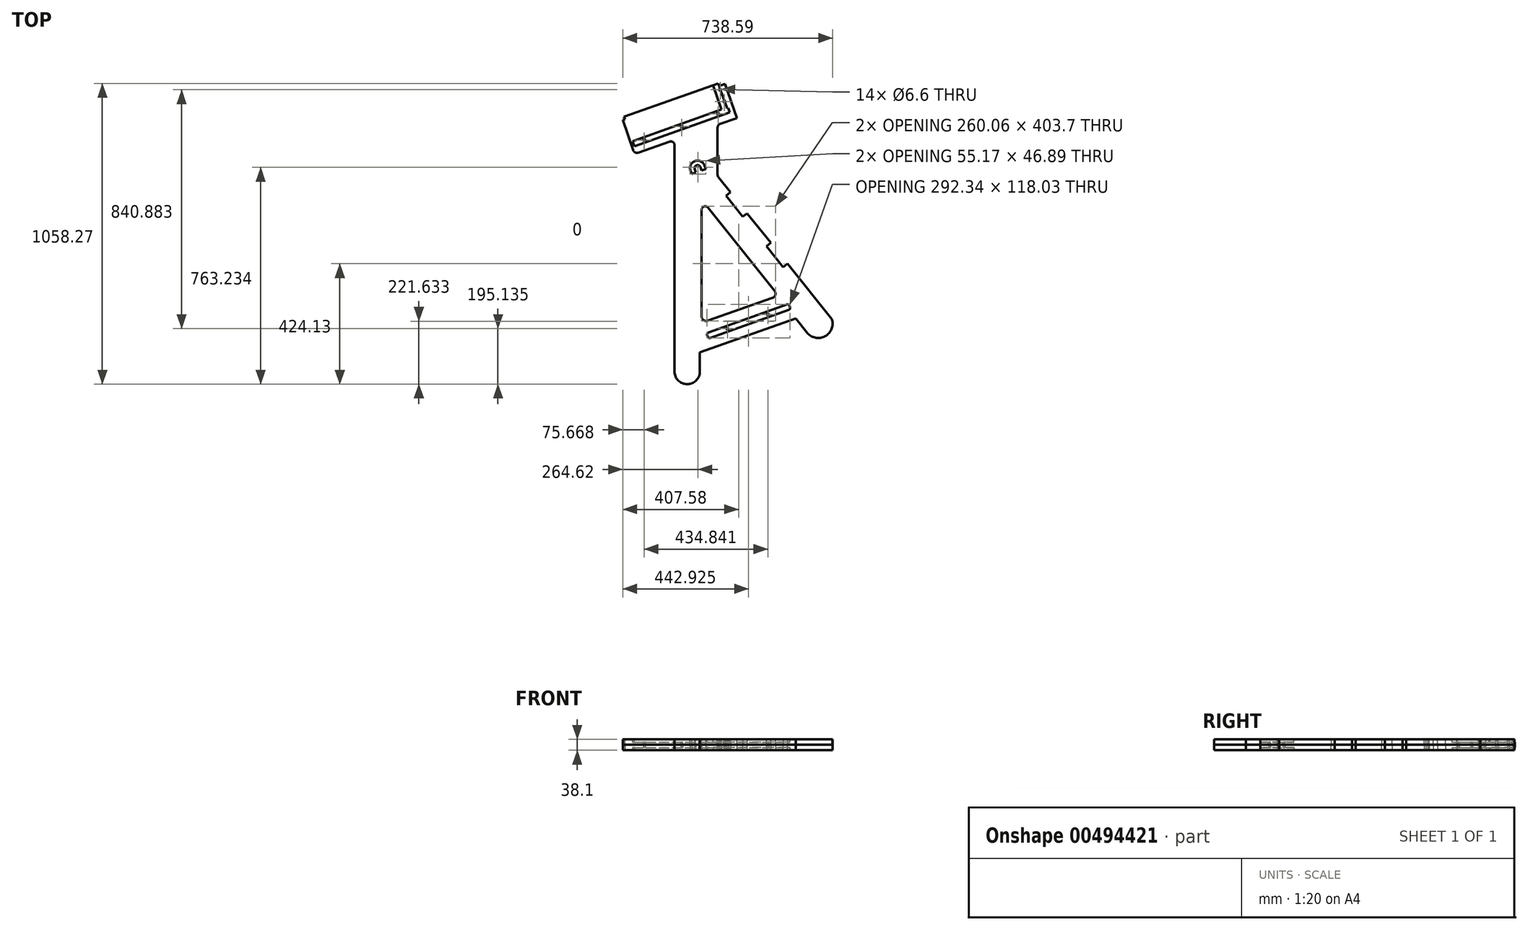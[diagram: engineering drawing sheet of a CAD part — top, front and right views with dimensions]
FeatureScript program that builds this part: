
annotation { "Feature Type Name" : "Feature", "Feature Type Description" : "" }
export const myFeature = defineFeature(function(context is Context, id is Id, definition is map)
    precondition{}
    {
        {
            var Q0;
            Q0=qCreatedBy(makeId("Top.planeOp"),FACE);
            var sketch = newSketch(context, id + "F0", { "sketchPlane" : qUnion([Q0])});
            skLineSegment(sketch, "E0", {"start": v(-306.62, -10.3) * mm, "end": v(-306.88, -10.27) * mm});
            skLineSegment(sketch, "E1", {"start": v(727.27, -289.32) * mm, "end": v(727.27, 507.63) * mm});
            skPoint(sketch, "E2.visualSharp", {"position": v(727.27, -334.1) * mm});
            skPoint(sketch, "E3.visualSharp", {"position": v(828.87, -334.66) * mm});
            skLineSegment(sketch, "E4", {"start": v(878.9, 569.94) * mm, "end": v(878.9, 402.04) * mm});
            skLineSegment(sketch, "E5", {"start": v(710.35, 519.6) * mm, "end": v(599.11, 480.45) * mm});
            skLineSegment(sketch, "E6", {"start": v(582.92, 488.22) * mm, "end": v(544.97, 596.03) * mm});
            skLineSegment(sketch, "E7", {"start": v(544.97, 596.03) * mm, "end": v(552.9, 598.83) * mm});
            skLineSegment(sketch, "E8", {"start": v(904.35, 722.53) * mm, "end": v(946.52, 602.74) * mm});
            skLineSegment(sketch, "E9", {"start": v(887.38, 581.92) * mm, "end": v(946.52, 602.74) * mm});
            skLineSegment(sketch, "E10", {"start": v(822.52, -95.2) * mm, "end": v(822.52, 279.38) * mm});
            skLineSegment(sketch, "E11", {"start": v(845.13, 287.31) * mm, "end": v(1078.98, -4.96) * mm});
            skPoint(sketch, "E12.visualSharp", {"position": v(822.52, 315.58) * mm});
            skArc(sketch, "E12.filletArc", {"start": v(845.13, 287.31) * mm, "mid": v(831.01, 291.36) * mm, "end": v(822.52, 279.38) * mm});
            skLineSegment(sketch, "E13", {"start": v(587.13, 476.24) * mm, "end": v(946.52, 602.74) * mm, "construction": true});
            skLineSegment(sketch, "E14", {"start": v(881.68, 394.1) * mm, "end": v(1281.26, -105.33) * mm});
            skArc(sketch, "E15", {"start": v(1192.97, -152.23) * mm, "mid": v(1256.56, -165.38) * mm, "end": v(1281.26, -105.33) * mm});
            skLineSegment(sketch, "E16", {"start": v(816.46, -289.32) * mm, "end": v(816.46, -221.63) * mm});
            skLineSegment(sketch, "E17", {"start": v(926.55, 733.52) * mm, "end": v(1268.68, -238.42) * mm, "construction": true});
            skPoint(sketch, "E18.visualSharp", {"position": v(878.9, 397.58) * mm});
            skArc(sketch, "E18.filletArc", {"start": v(878.9, 402.04) * mm, "mid": v(879.61, 397.83) * mm, "end": v(881.68, 394.1) * mm});
            skPoint(sketch, "E19.visualSharp", {"position": v(878.9, 578.94) * mm});
            skArc(sketch, "E19.filletArc", {"start": v(887.38, 581.92) * mm, "mid": v(881.23, 577.28) * mm, "end": v(878.9, 569.94) * mm});
            skArc(sketch, "E20.filletArc", {"start": v(727.27, 507.63) * mm, "mid": v(721.9, 518) * mm, "end": v(710.35, 519.6) * mm});
            skLineSegment(sketch, "E21", {"start": v(549.74, 607.81) * mm, "end": v(880.86, 724.36) * mm});
            skLineSegment(sketch, "E22", {"start": v(549.74, 607.81) * mm, "end": v(552.9, 598.83) * mm});
            skLineSegment(sketch, "E23", {"start": v(880.86, 724.36) * mm, "end": v(884.02, 715.38) * mm});
            skLineSegment(sketch, "E24.trimOffspring", {"start": v(884.02, 715.38) * mm, "end": v(904.35, 722.53) * mm, "construction": true});
            skLineSegment(sketch, "E25.trimOffspring", {"start": v(884.02, 715.38) * mm, "end": v(904.35, 722.53) * mm});
            skLineSegment(sketch, "E26", {"start": v(544.97, 596.03) * mm, "end": v(903.18, -421.63) * mm, "construction": true});
            skLineSegment(sketch, "E27", {"start": v(869.21, -325.12) * mm, "end": v(1232.7, -197.18) * mm, "construction": true});
            skLineSegment(sketch, "E28", {"start": v(816.46, -221.63) * mm, "end": v(1153.56, -102.97) * mm});
            skLineSegment(sketch, "E29", {"start": v(844.5, -110.78) * mm, "end": v(1071.57, -30.85) * mm});
            skArc(sketch, "E30", {"start": v(727.27, -289.32) * mm, "mid": v(771.86, -333.91) * mm, "end": v(816.46, -289.32) * mm});
            skPoint(sketch, "E31.visualSharp", {"position": v(587.13, 476.24) * mm});
            skArc(sketch, "E31.filletArc", {"start": v(582.92, 488.22) * mm, "mid": v(589.4, 480.98) * mm, "end": v(599.11, 480.45) * mm});
            skPoint(sketch, "E32.visualSharp", {"position": v(1093.5, -23.13) * mm});
            skArc(sketch, "E32.filletArc", {"start": v(1071.57, -30.85) * mm, "mid": v(1081.96, -19.82) * mm, "end": v(1078.98, -4.96) * mm});
            skPoint(sketch, "E33.visualSharp", {"position": v(822.52, -118.52) * mm});
            skArc(sketch, "E33.filletArc", {"start": v(822.52, -95.2) * mm, "mid": v(829.49, -108.68) * mm, "end": v(844.5, -110.78) * mm});
            skLineSegment(sketch, "E34", {"start": v(1153.56, -102.97) * mm, "end": v(1192.97, -152.23) * mm});
            skPoint(sketch, "E35", {"position": v(1256.56, -165.38) * mm});
            skPoint(sketch, "E36", {"position": v(771.86, -333.91) * mm});
            skPoint(sketch, "E37", {"position": v(1272.05, -152.68) * mm});
            skLineSegment(sketch, "E38", {"start": v(786.67, -331.38) * mm, "end": v(1249.58, -168.44) * mm, "construction": true});
            skArc(sketch, "E39", {"start": v(817.98, 430.01) * mm, "mid": v(804.77, 436.34) * mm, "end": v(798.43, 423.13) * mm});
            skArc(sketch, "E40", {"start": v(832.96, 435.28) * mm, "mid": v(799.5, 451.32) * mm, "end": v(783.46, 417.86) * mm});
            skLineSegment(sketch, "E41", {"start": v(783.46, 417.86) * mm, "end": v(787.67, 405.88) * mm});
            skLineSegment(sketch, "E42", {"start": v(787.67, 405.88) * mm, "end": v(802.65, 411.15) * mm});
            skLineSegment(sketch, "E43", {"start": v(802.65, 411.15) * mm, "end": v(798.43, 423.13) * mm});
            skLineSegment(sketch, "E44", {"start": v(817.98, 430.01) * mm, "end": v(822.2, 418.03) * mm});
            skLineSegment(sketch, "E45", {"start": v(822.2, 418.03) * mm, "end": v(837.17, 423.3) * mm});
            skLineSegment(sketch, "E46", {"start": v(837.17, 423.3) * mm, "end": v(832.96, 435.28) * mm});
            skSolve(sketch);
        }
        {
            var Q0;
            Q0=makeQuery(id+"F0.imprint","IMPRINT",FACE,{"disambiguationData":[TD([[makeQuery(id+"F0.imprint","IMPRINT",EDGE,{"derivedFrom":sQuery(id+"F0.wireOp",EDGE,"oAVC5DI8-kh1G-Qbfy-uwvq-Txyh6lFHP0Ui")}),1.0]])]});
            var Q1;
            Q1=makeQuery(id+"F0.imprint","IMPRINT",FACE,{"disambiguationData":[TD([[makeQuery(id+"F0.imprint","IMPRINT",EDGE,{"derivedFrom":sQuery(id+"F0.wireOp",EDGE,"E1")}),-1.0]])]});
            extrude(context, id + "F1", {"entities" : qUnion([Q0, Q1]), "depth" : 19.05 * mm});
        }
        {
            var Q0;
            {var subQ2=sQuery(id+"F0.wireOp",EDGE,"E1");Q0=makeQuery(id+"F0.imprint","IMPRINT",FACE,{"disambiguationData":[TD([[makeQuery(id+"F0.imprint","IMPRINT",EDGE,{"derivedFrom":subQ2}),-1.0]])]});}
            var sketch = newSketch(context, id + "F2", { "sketchPlane" : qUnion([Q0])});
            skLineSegment(sketch, "E47", {"start": v(852.3, -170.94) * mm, "end": v(1129.86, -72.11) * mm});
            skLineSegment(sketch, "E48", {"start": v(1123.5, -53.62) * mm, "end": v(845.93, -152.44) * mm});
            skLineSegment(sketch, "E49", {"start": v(1133.77, -64.18) * mm, "end": v(1131.67, -57.65) * mm});
            skLineSegment(sketch, "E50", {"start": v(844.12, -166.9) * mm, "end": v(842.02, -160.38) * mm});
            skPoint(sketch, "E51.visualSharp", {"position": v(846.13, -173.13) * mm});
            skArc(sketch, "E51.filletArc", {"start": v(844.12, -166.9) * mm, "mid": v(847.36, -170.65) * mm, "end": v(852.3, -170.94) * mm});
            skPoint(sketch, "E52.visualSharp", {"position": v(840.12, -154.51) * mm});
            skArc(sketch, "E52.filletArc", {"start": v(845.93, -152.44) * mm, "mid": v(842.36, -155.62) * mm, "end": v(842.02, -160.38) * mm});
            skPoint(sketch, "E53.visualSharp", {"position": v(1135.67, -70.04) * mm});
            skArc(sketch, "E53.filletArc", {"start": v(1129.86, -72.11) * mm, "mid": v(1133.43, -68.94) * mm, "end": v(1133.77, -64.18) * mm});
            skPoint(sketch, "E54.visualSharp", {"position": v(1129.66, -51.42) * mm});
            skArc(sketch, "E54.filletArc", {"start": v(1131.67, -57.65) * mm, "mid": v(1128.43, -53.9) * mm, "end": v(1123.5, -53.62) * mm});
            skSolve(sketch);
        }
        {
            var Q0;
            Q0=qSketchRegion(id+"F2",true);
            extrude(context, id + "F3", {"entities" : qUnion([Q0]), "operationType" : NewBodyOperationType.REMOVE, "depth" : 9.52 * mm});
        }
        {
            var Q0;
            {var subQ2=sQuery(id+"F0.wireOp",EDGE,"E1");Q0=makeQuery(id+"F0.imprint","IMPRINT",FACE,{"disambiguationData":[TD([[makeQuery(id+"F0.imprint","IMPRINT",EDGE,{"derivedFrom":subQ2}),-1.0]])]});}
            var sketch = newSketch(context, id + "F4", { "sketchPlane" : qUnion([Q0])});
            skLineSegment(sketch, "E55.bottom", {"start": v(586.5, 502.94) * mm, "end": v(921.88, 622.35) * mm});
            skLineSegment(sketch, "E55.top", {"start": v(579.94, 521.37) * mm, "end": v(892.72, 632.73) * mm});
            skLineSegment(sketch, "E55.left", {"start": v(586.5, 502.94) * mm, "end": v(579.94, 521.37) * mm});
            skLineSegment(sketch, "E56", {"start": v(862.38, 717.95) * mm, "end": v(892.72, 632.73) * mm});
            skPoint(sketch, "E57.0", {"position": v(884.02, 715.38) * mm});
            skPoint(sketch, "E58.0", {"position": v(880.86, 724.36) * mm});
            skLineSegment(sketch, "E59", {"start": v(880.86, 724.36) * mm, "end": v(884.02, 715.38) * mm});
            skLineSegment(sketch, "E60", {"start": v(880.86, 724.36) * mm, "end": v(862.38, 717.95) * mm});
            skLineSegment(sketch, "E61", {"start": v(912.13, 636.43) * mm, "end": v(884.02, 715.38) * mm});
            skLineSegment(sketch, "E62", {"start": v(912.13, 636.43) * mm, "end": v(916.33, 637.93) * mm});
            skLineSegment(sketch, "E63", {"start": v(921.88, 622.35) * mm, "end": v(916.33, 637.93) * mm});
            skSolve(sketch);
        }
        {
            var Q0;
            Q0=qSketchRegion(id+"F4",true);
            extrude(context, id + "F5", {"entities" : qUnion([Q0]), "operationType" : NewBodyOperationType.REMOVE, "depth" : 9.52 * mm});
        }
        {
            var Q0;
            Q0=makeQuery(id+"F1.opExtrude","SWEPT_FACE",FACE,{"disambiguationData":[OSD([sQuery(id+"F0.wireOp",EDGE,"E14")])]});
            var sketch = newSketch(context, id + "F6", { "sketchPlane" : qUnion([Q0])});
            skLineSegment(sketch, "E64", {"start": v(-310.5, 19.05) * mm, "end": v(-310.5, 0) * mm});
            skLineSegment(sketch, "E65", {"start": v(-310.5, 0) * mm, "end": v(-405.25, 0) * mm});
            skLineSegment(sketch, "E66", {"start": v(-405.25, 0) * mm, "end": v(-405.25, 19.05) * mm});
            skLineSegment(sketch, "E67", {"start": v(-405.25, 19.05) * mm, "end": v(-310.5, 19.05) * mm});
            skLineSegment(sketch, "E68", {"start": v(-537.62, 21.33) * mm, "end": v(-537.62, -0.7) * mm});
            skLineSegment(sketch, "E69", {"start": v(-537.62, -0.7) * mm, "end": v(-632.36, -0.7) * mm});
            skLineSegment(sketch, "E70", {"start": v(-632.36, -0.7) * mm, "end": v(-632.36, 21.33) * mm});
            skLineSegment(sketch, "E71", {"start": v(-632.36, 21.33) * mm, "end": v(-537.62, 21.33) * mm});
            skSolve(sketch);
        }
        {
            var Q0;
            Q0=qSketchRegion(id+"F6",true);
            extrude(context, id + "F7", {"entities" : qUnion([Q0]), "operationType" : NewBodyOperationType.REMOVE, "oppositeDirection" : true, "depth" : 19.56 * mm});
        }
        {
            var Q0;
            Q0=makeQuery(id+"F0.imprint","IMPRINT",FACE,{"disambiguationData":[TD([[makeQuery(id+"F0.imprint","IMPRINT",EDGE,{"derivedFrom":sQuery(id+"F0.wireOp",EDGE,"E1")}),-1.0]])]});
            var sketch = newSketch(context, id + "F8", { "sketchPlane" : qUnion([Q0])});
            skLineSegment(sketch, "E72", {"start": v(916.91, 620.58) * mm, "end": v(879.28, 726.3) * mm, "construction": true});
            skLineSegment(sketch, "E73.0", {"start": v(912.13, 636.43) * mm, "end": v(884.02, 715.38) * mm});
            skCircle(sketch, "E74", {"center": v(902.66, 660.61) * mm, "radius": 3.3 * mm});
            skCircle(sketch, "E75", {"center": v(887.92, 702.1) * mm, "radius": 3.3 * mm});
            skLineSegment(sketch, "E76", {"start": v(921.57, 632.52) * mm, "end": v(583.89, 512.3) * mm, "construction": true});
            skCircle(sketch, "E77", {"center": v(880.54, 617.91) * mm, "radius": 3.3 * mm});
            skCircle(sketch, "E78", {"center": v(620.64, 525.38) * mm, "radius": 3.3 * mm});
            skCircle(sketch, "E79", {"center": v(752.73, 572.4) * mm, "radius": 3.3 * mm});
            skLineSegment(sketch, "E80.0", {"start": v(1133.77, -64.18) * mm, "end": v(1131.67, -57.65) * mm});
            skLineSegment(sketch, "E81.0", {"start": v(1123.5, -53.62) * mm, "end": v(845.93, -152.44) * mm});
            skLineSegment(sketch, "E82", {"start": v(1123.33, -64.1) * mm, "end": v(843.4, -163.77) * mm, "construction": true});
            skCircle(sketch, "E83", {"center": v(1055.48, -88.26) * mm, "radius": 3.3 * mm});
            skCircle(sketch, "E84", {"center": v(913.6, -138.78) * mm, "radius": 3.3 * mm});
            skLineSegment(sketch, "E85", {"start": v(752.73, 572.4) * mm, "end": v(620.64, 525.38) * mm});
            skSolve(sketch);
        }
        {
            var Q0;
            Q0=qSketchRegion(id+"F8",true);
            extrude(context, id + "F9", {"entities" : qUnion([Q0]), "operationType" : NewBodyOperationType.REMOVE, "endBound" : BoundingType.THROUGH_ALL, "depth" : 25.4 * mm});
        }
        {
            var Q0;
            Q0=sQuery(id+"F0.wireOp",EDGE,"E40");
            var Q1;
            Q1=sQuery(id+"F0.wireOp",EDGE,"E46");
            var Q2;
            Q2=sQuery(id+"F0.wireOp",EDGE,"E39");
            var Q3;
            Q3=sQuery(id+"F0.wireOp",EDGE,"E44");
            var Q4;
            Q4=sQuery(id+"F0.wireOp",EDGE,"E45");
            var Q5;
            Q5=sQuery(id+"F0.wireOp",EDGE,"E43");
            var Q6;
            Q6=sQuery(id+"F0.wireOp",EDGE,"E41");
            var Q7;
            Q7=sQuery(id+"F0.wireOp",EDGE,"E42");
            extrude(context, id + "F10", {"bodyType" : ToolBodyType.SURFACE, "surfaceEntities" : qUnion([Q0, Q1, Q2, Q3, Q4, Q5, Q6, Q7]), "depth" : 25.4 * mm});
        }
        {
            var Q0;
            Q0=makeQuery(id+"F1.opExtrude","CAP_FACE",FACE,{"disambiguationData":[OSD([sQuery(id+"F0.wireOp",EDGE,"E1"),sQuery(id+"F0.wireOp",EDGE,"E4"),sQuery(id+"F0.wireOp",EDGE,"E5"),sQuery(id+"F0.wireOp",EDGE,"E6"),sQuery(id+"F0.wireOp",EDGE,"E7"),sQuery(id+"F0.wireOp",EDGE,"E8"),sQuery(id+"F0.wireOp",EDGE,"E9"),sQuery(id+"F0.wireOp",EDGE,"E10"),sQuery(id+"F0.wireOp",EDGE,"E11"),sQuery(id+"F0.wireOp",EDGE,"E12.filletArc"),sQuery(id+"F0.wireOp",EDGE,"E14"),sQuery(id+"F0.wireOp",EDGE,"E15"),sQuery(id+"F0.wireOp",EDGE,"E16"),sQuery(id+"F0.wireOp",EDGE,"E18.filletArc"),sQuery(id+"F0.wireOp",EDGE,"E19.filletArc"),sQuery(id+"F0.wireOp",EDGE,"E20.filletArc"),sQuery(id+"F0.wireOp",EDGE,"E21"),sQuery(id+"F0.wireOp",EDGE,"E22"),sQuery(id+"F0.wireOp",EDGE,"E23"),sQuery(id+"F0.wireOp",EDGE,"E25.trimOffspring"),sQuery(id+"F0.wireOp",EDGE,"E28"),sQuery(id+"F0.wireOp",EDGE,"E29"),sQuery(id+"F0.wireOp",EDGE,"E30"),sQuery(id+"F0.wireOp",EDGE,"E31.filletArc"),sQuery(id+"F0.wireOp",EDGE,"E32.filletArc"),sQuery(id+"F0.wireOp",EDGE,"E33.filletArc"),sQuery(id+"F0.wireOp",EDGE,"E34"),sQuery(id+"F0.wireOp",EDGE,"E39"),sQuery(id+"F0.wireOp",EDGE,"E40"),sQuery(id+"F0.wireOp",EDGE,"E41"),sQuery(id+"F0.wireOp",EDGE,"E42"),sQuery(id+"F0.wireOp",EDGE,"E43"),sQuery(id+"F0.wireOp",EDGE,"E44"),sQuery(id+"F0.wireOp",EDGE,"E45"),sQuery(id+"F0.wireOp",EDGE,"E46")])],"isStart":false});
            var sketch = newSketch(context, id + "F11", { "sketchPlane" : qUnion([Q0])});
            skLineSegment(sketch, "E86", {"start": v(544.97, 596.03) * mm, "end": v(771.86, -333.91) * mm, "construction": true});
            skLineSegment(sketch, "E87", {"start": v(771.86, -333.91) * mm, "end": v(1697.98, 265.87) * mm, "construction": true});
            skLineSegment(sketch, "E88", {"start": v(1697.98, 265.87) * mm, "end": v(1633.87, 296.9) * mm, "construction": true});
            skSolve(sketch);
        }
        {
            var Q0;
            Q0=makeQuery(id+"F1.opExtrude","SWEPT_BODY",BODY,{"disambiguationData":[OSD([sQuery(id+"F0.wireOp",EDGE,"E1"),sQuery(id+"F0.wireOp",EDGE,"E4"),sQuery(id+"F0.wireOp",EDGE,"E5"),sQuery(id+"F0.wireOp",EDGE,"E6"),sQuery(id+"F0.wireOp",EDGE,"E7"),sQuery(id+"F0.wireOp",EDGE,"E8"),sQuery(id+"F0.wireOp",EDGE,"E9"),sQuery(id+"F0.wireOp",EDGE,"E10"),sQuery(id+"F0.wireOp",EDGE,"E11"),sQuery(id+"F0.wireOp",EDGE,"E12.filletArc"),sQuery(id+"F0.wireOp",EDGE,"E14"),sQuery(id+"F0.wireOp",EDGE,"E15"),sQuery(id+"F0.wireOp",EDGE,"E16"),sQuery(id+"F0.wireOp",EDGE,"E18.filletArc"),sQuery(id+"F0.wireOp",EDGE,"E19.filletArc"),sQuery(id+"F0.wireOp",EDGE,"E20.filletArc"),sQuery(id+"F0.wireOp",EDGE,"E21"),sQuery(id+"F0.wireOp",EDGE,"E22"),sQuery(id+"F0.wireOp",EDGE,"E23"),sQuery(id+"F0.wireOp",EDGE,"E25.trimOffspring"),sQuery(id+"F0.wireOp",EDGE,"E28"),sQuery(id+"F0.wireOp",EDGE,"E29"),sQuery(id+"F0.wireOp",EDGE,"E30"),sQuery(id+"F0.wireOp",EDGE,"E31.filletArc"),sQuery(id+"F0.wireOp",EDGE,"E32.filletArc"),sQuery(id+"F0.wireOp",EDGE,"E33.filletArc"),sQuery(id+"F0.wireOp",EDGE,"E34"),sQuery(id+"F0.wireOp",EDGE,"E39"),sQuery(id+"F0.wireOp",EDGE,"E40"),sQuery(id+"F0.wireOp",EDGE,"E41"),sQuery(id+"F0.wireOp",EDGE,"E42"),sQuery(id+"F0.wireOp",EDGE,"E43"),sQuery(id+"F0.wireOp",EDGE,"E44"),sQuery(id+"F0.wireOp",EDGE,"E45"),sQuery(id+"F0.wireOp",EDGE,"E46")])]});
            var Q1;
            {var subQ34=sQuery(id+"F0.wireOp",EDGE,"E1");Q1=makeQuery(id+"F11.imprint","IMPRINT",FACE,{"disambiguationData":[TD([[makeQuery(id+"F11.imprint","IMPRINT",EDGE,{"derivedFrom":makeQuery(id+"F1.opExtrude","CAP_EDGE",EDGE,{"disambiguationData":[OSD([subQ34])],"isStart":false})}),-1.0]])]});}
            mirror(context, id + "F12", {"entities" : qUnion([Q0]), "mirrorPlane" : qUnion([Q1])});
        }
    });
